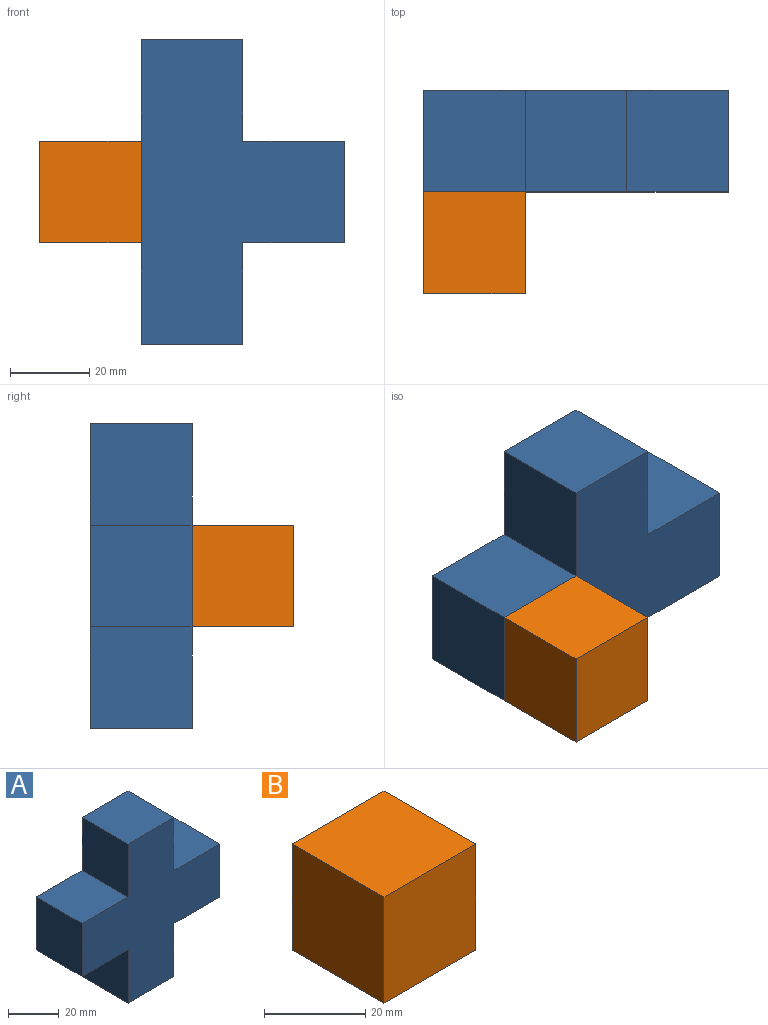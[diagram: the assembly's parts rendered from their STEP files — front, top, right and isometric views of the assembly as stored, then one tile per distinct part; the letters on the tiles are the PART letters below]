
ASSEMBLY  parts=2 mates=1
PART A: 14 faces, bbox 76.9x25.7x76.9 mm
  f0: plane 25.65x25.64mm, normal (-1,0,0), area 657.8mm2, adj f1,f11,f12,f13
  f1: plane 25.65x25.64mm, normal (0,0,1), area 657.8mm2, adj f0,f2,f12,f13
  f2: plane 25.65x25.64mm, normal (-1,0,0), area 657.8mm2, adj f1,f3,f12,f13
  f3: plane 25.65x25.64mm, normal (0,0,-1), area 657.8mm2, adj f2,f4,f12,f13
  f4: plane 25.65x25.64mm, normal (-1,0,0), area 657.8mm2, adj f3,f5,f12,f13
  f5: plane 25.65x25.64mm, normal (0,0,-1), area 657.8mm2, adj f4,f6,f12,f13
  f6: plane 25.65x25.64mm, normal (1,0,0), area 657.8mm2, adj f5,f7,f12,f13
  f7: plane 25.65x25.64mm, normal (0,0,-1), area 657.8mm2, adj f6,f8,f12,f13
  f8: plane 25.65x25.64mm, normal (1,0,0), area 657.8mm2, adj f7,f9,f12,f13
  f9: plane 25.65x25.64mm, normal (0,0,1), area 657.8mm2, adj f8,f10,f12,f13
  f10: plane 25.65x25.64mm, normal (1,0,0), area 657.8mm2, adj f9,f11,f12,f13
  f11: plane 25.65x25.64mm, normal (0,0,1), area 657.8mm2, adj f0,f10,f12,f13
  f12: plane 76.93x76.93mm, normal (0,-1,0), area 3287.7mm2, adj f0,f1,f2,f3,f4,f5,f6,f7
  f13: plane 76.93x76.93mm, normal (0,1,0), area 3287.7mm2, adj f0,f1,f2,f3,f4,f5,f6,f7
PART B: 6 faces, bbox 25.7x25.7x25.7 mm
  f0: plane 25.65x25.65mm, normal (0,0,-1), area 658.1mm2, adj f1,f3,f4,f5
  f1: plane 25.65x25.65mm, normal (1,0,0), area 658.1mm2, adj f0,f2,f4,f5
  f2: plane 25.65x25.65mm, normal (0,0,1), area 658.1mm2, adj f1,f3,f4,f5
  f3: plane 25.65x25.65mm, normal (-1,0,0), area 658.1mm2, adj f0,f2,f4,f5
  f4: plane 25.65x25.65mm, normal (0,-1,0), area 658.1mm2, adj f0,f1,f2,f3
  f5: plane 25.65x25.65mm, normal (0,1,0), area 658.1mm2, adj f0,f1,f2,f3
PLACE A rot(axis=(-0.3,0.25,0.92),0deg) t=(-17.76,-3.01,6.83)mm
PLACE B rot(axis=(-0.3,0.25,0.92),0deg) t=(-65.84,-28.66,11.26)mm
MATE fastened A.f2 <-> B.f3  axis (-1,0,0) through (-78.66,-15.83,11.26)mm
